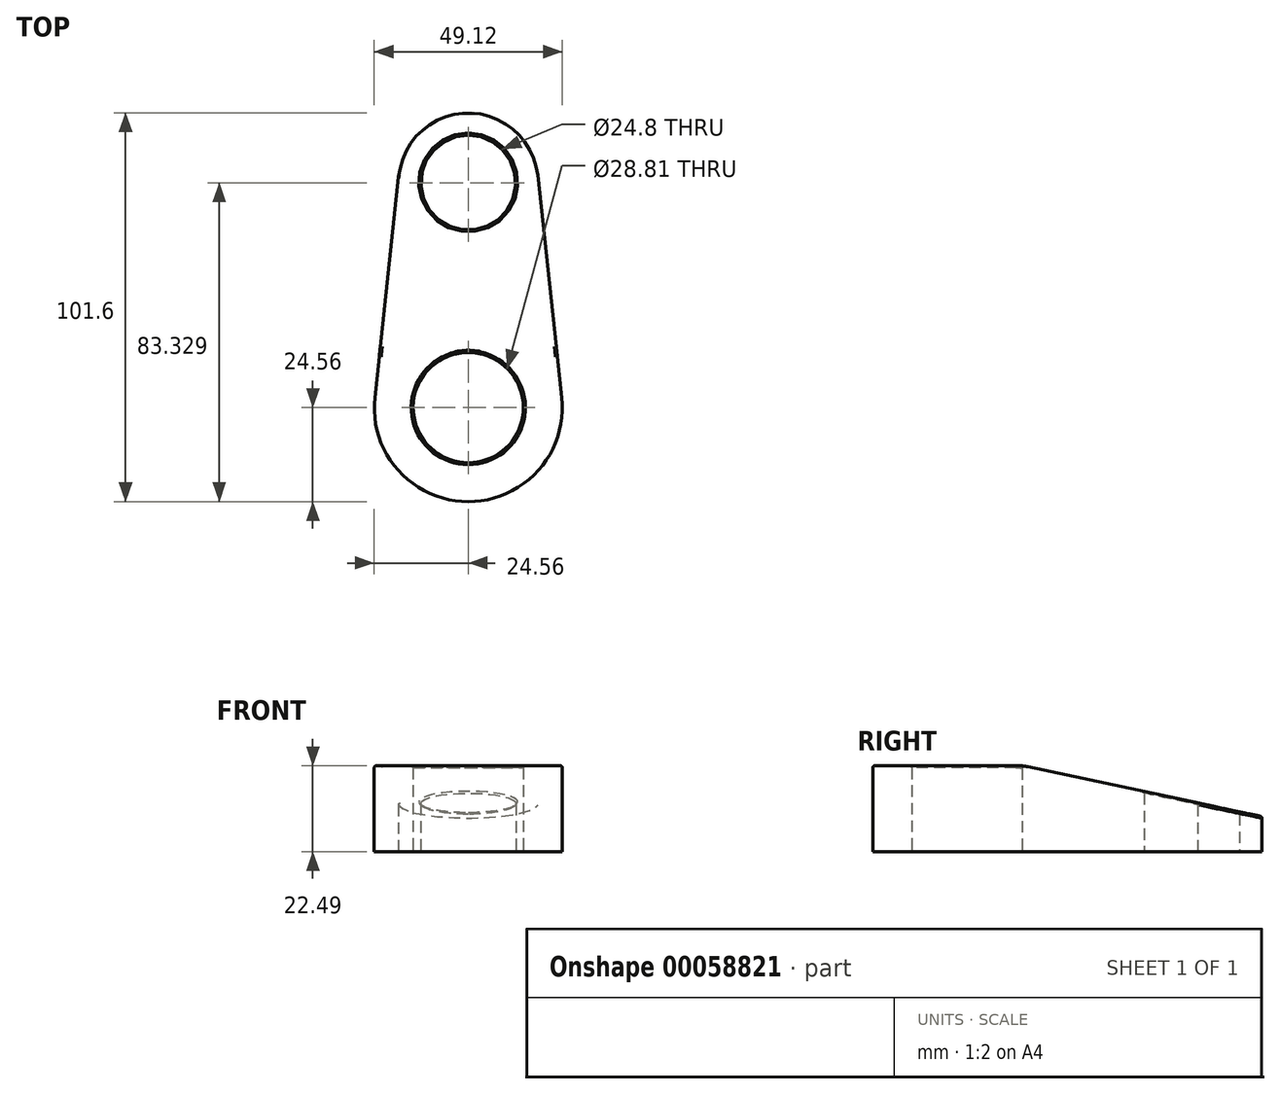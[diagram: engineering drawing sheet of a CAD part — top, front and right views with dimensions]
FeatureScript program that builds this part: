
annotation { "Feature Type Name" : "Feature", "Feature Type Description" : "" }
export const myFeature = defineFeature(function(context is Context, id is Id, definition is map)
    precondition{}
    {
        {
            var Q0;
            Q0=qCreatedBy(makeId("Top.planeOp"),FACE);
            var sketch = newSketch(context, id + "F0", { "sketchPlane" : qUnion([Q0])});
            skCircle(sketch, "E0", {"center": v(0, 0) * mm, "radius": 24.56 * mm});
            skCircle(sketch, "E1", {"center": v(0, 0) * mm, "radius": 14.4 * mm});
            skCircle(sketch, "E2", {"center": v(0, 58.77) * mm, "radius": 18.27 * mm});
            skCircle(sketch, "E3", {"center": v(0, 58.77) * mm, "radius": 12.4 * mm});
            skLineSegment(sketch, "E4", {"start": v(-18.1, 61.2) * mm, "end": v(-24.7, 0) * mm});
            skLineSegment(sketch, "E5", {"start": v(18.16, 60.73) * mm, "end": v(24.7, 0) * mm});
            skSolve(sketch);
        }
        {
            var Q0;
            Q0 = qSketchRegion(id + "F0", true);
            extrude(context, id + "F1", {"entities" : qUnion([Q0]), "depth" : 22.49 * mm});
        }
        {
            var Q0;
            Q0=qCreatedBy(makeId("Right.planeOp"),FACE);
            var sketch = newSketch(context, id + "F2", { "sketchPlane" : qUnion([Q0])});
            skLineSegment(sketch, "E6", {"start": v(0, 0) * mm, "end": v(0, 22.6) * mm, "construction": true});
            skLineSegment(sketch, "E7", {"start": v(0, 22.6) * mm, "end": v(14.05, 22.6) * mm, "construction": true});
            skLineSegment(sketch, "E8", {"start": v(14.05, 22.6) * mm, "end": v(87.92, 22.6) * mm});
            skLineSegment(sketch, "E9", {"start": v(87.92, 22.6) * mm, "end": v(87.92, 6.9) * mm});
            skLineSegment(sketch, "E10", {"start": v(87.92, 6.9) * mm, "end": v(14.05, 22.6) * mm});
            skSolve(sketch);
        }
        {
            var Q0;
            Q0 = qSketchRegion(id + "F2", true);
            extrude(context, id + "F3", {"entities" : qUnion([Q0]), "operationType" : NewBodyOperationType.REMOVE, "endBound" : BoundingType.SYMMETRIC, "oppositeDirection" : true, "depth" : 50.8 * mm});
        }
        {
            var Q0;
            Q0=makeQuery(id+"F3.boolean.opBoolean","INTERSECT",EDGE,{"derivedFrom":[makeQuery(id+"F1.opExtrude","CAP_FACE",FACE,{"disambiguationData":[OSD([sQuery(id+"F0.wireOp",EDGE,"E0"),sQuery(id+"F0.wireOp",EDGE,"E1"),sQuery(id+"F0.wireOp",EDGE,"E2"),sQuery(id+"F0.wireOp",EDGE,"E3"),sQuery(id+"F0.wireOp",EDGE,"E4"),sQuery(id+"F0.wireOp",EDGE,"E5")])],"isStart":false}),makeQuery(id+"F3.opExtrude","SWEPT_FACE",FACE,{"disambiguationData":[OSD([sQuery(id+"F2.wireOp",EDGE,"E10")])]})]});
            fillet(context, id + "F4", {"entities" : qUnion([Q0]), "radius" : 12.7 * mm, "tangentPropagation" : true, "allowEdgeOverflow" : false});
        }
        {
            var Q0;
            Q0=makeQuery(id+"F1.opExtrude","CAP_EDGE",EDGE,{"disambiguationData":[OSD([sQuery(id+"F0.wireOp",EDGE,"E0")])],"isStart":false});
            fillet(context, id + "F5", {"entities" : qUnion([Q0]), "radius" : 0.5 * mm, "tangentPropagation" : true, "allowEdgeOverflow" : false});
        }
        {
            var Q0;
            Q0=makeQuery(id+"F1.opExtrude","CAP_EDGE",EDGE,{"disambiguationData":[OSD([sQuery(id+"F0.wireOp",EDGE,"E1")])],"isStart":false});
            var Q1;
            Q1=makeQuery(id+"F3.boolean.opBoolean","INTERSECT",EDGE,{"derivedFrom":[makeQuery(id+"F1.opExtrude","SWEPT_FACE",FACE,{"disambiguationData":[OSD([sQuery(id+"F0.wireOp",EDGE,"E3")])]}),makeQuery(id+"F3.opExtrude","SWEPT_FACE",FACE,{"disambiguationData":[OSD([sQuery(id+"F2.wireOp",EDGE,"E10")])]})]});
            chamfer(context, id + "F6", {"entities" : qUnion([Q0, Q1]), "width" : 0.5 * mm, "tangentPropagation" : true});
        }
    });
